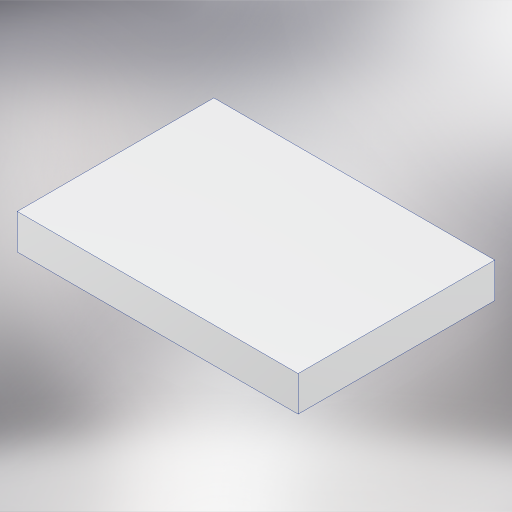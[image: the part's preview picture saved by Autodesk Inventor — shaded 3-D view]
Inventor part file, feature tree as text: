
AUTODESK INVENTOR PART (.ipt)
format: ipt  version: 2024 (Build 280153000, 153)  size: 257,536 bytes
history: native  units: in
note: dims shown in document units (in); Inventor stores cm internally (conversion verified against a paired STEP export)
features: extrude x1, sketch x1
ambient origin geometry x8: Origin, YZ Plane, XZ Plane, XY Plane, X Axis, Y Axis, Z Axis, Center Point
bodies: Solid1 (feature_tree)
feature tree (2):
  extrude  "Extrusion1"  Depth=1.5748in
  sketch  "Sketch1"  dims[d0=1.1024in d1=1.5748in d2=0.1969in d3=0.0in]
